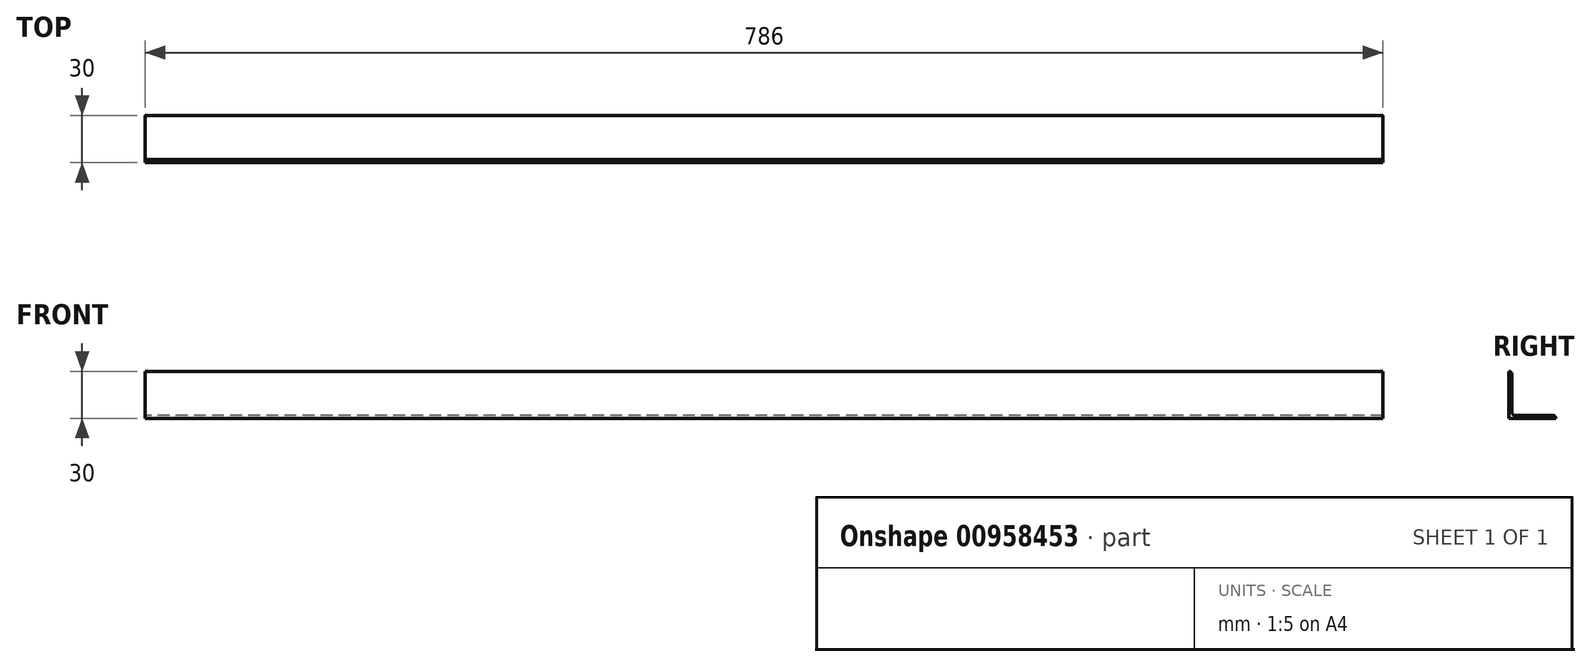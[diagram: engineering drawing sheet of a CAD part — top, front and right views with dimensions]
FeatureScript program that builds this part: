
annotation { "Feature Type Name" : "Feature", "Feature Type Description" : "" }
export const myFeature = defineFeature(function(context is Context, id is Id, definition is map)
    precondition{}
    {
        {
            var Q0;
            Q0=qCreatedBy(makeId("Right.planeOp"),FACE);
            var sketch = newSketch(context, id + "F0", { "sketchPlane" : qUnion([Q0])});
            skLineSegment(sketch, "E0", {"start": v(0, 0) * mm, "end": v(0, 30) * mm});
            skLineSegment(sketch, "E1", {"start": v(0, 0) * mm, "end": v(30, 0) * mm});
            skLineSegment(sketch, "E2.0", {"start": v(2, 4) * mm, "end": v(2, 28) * mm});
            skLineSegment(sketch, "E2.1", {"start": v(4, 2) * mm, "end": v(28, 2) * mm});
            skLineSegment(sketch, "E3", {"start": v(30, 0) * mm, "end": v(30, 0) * mm});
            skLineSegment(sketch, "E4", {"start": v(0, 30) * mm, "end": v(0, 30) * mm});
            skPoint(sketch, "E5.visualSharp", {"position": v(2, 30) * mm});
            skArc(sketch, "E5.filletArc", {"start": v(2, 28) * mm, "mid": v(1.41, 29.41) * mm, "end": v(0, 30) * mm});
            skPoint(sketch, "E6.visualSharp", {"position": v(30, 2) * mm});
            skArc(sketch, "E6.filletArc", {"start": v(30, 0) * mm, "mid": v(29.41, 1.41) * mm, "end": v(28, 2) * mm});
            skPoint(sketch, "E7.visualSharp", {"position": v(2, 2) * mm});
            skArc(sketch, "E7.filletArc", {"start": v(2, 4) * mm, "mid": v(2.59, 2.59) * mm, "end": v(4, 2) * mm});
            skSolve(sketch);
        }
        {
            var Q0;
            Q0=makeQuery(id+"F0.imprint","IMPRINT",FACE,{"disambiguationData":[TD([[makeQuery(id+"F0.imprint","IMPRINT",EDGE,{"derivedFrom":sQuery(id+"F0.wireOp",EDGE,"E0")}),-1.0]])]});
            extrude(context, id + "F1", {"entities" : qUnion([Q0]), "depth" : 786 * mm, "offsetDistance" : 25 * mm});
        }
    });
